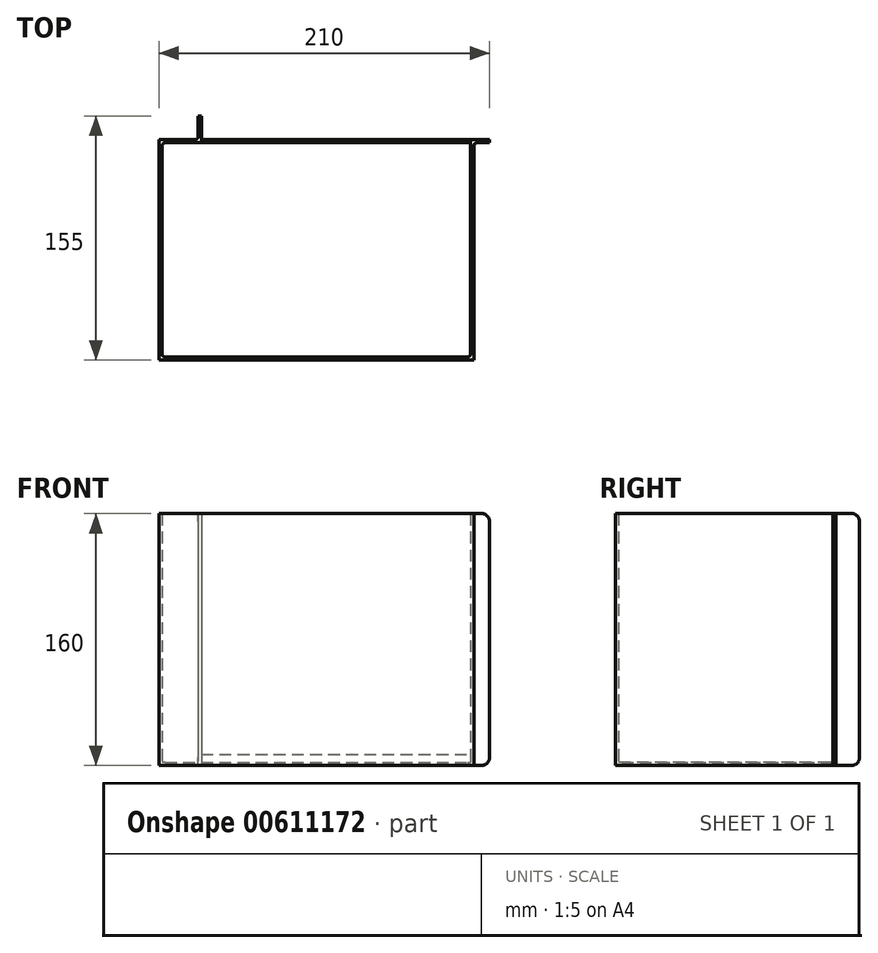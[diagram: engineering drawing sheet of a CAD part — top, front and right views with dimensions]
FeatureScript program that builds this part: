
annotation { "Feature Type Name" : "Feature", "Feature Type Description" : "" }
export const myFeature = defineFeature(function(context is Context, id is Id, definition is map)
    precondition{}
    {
        {
            var Q0;
            Q0=qCreatedBy(makeId("Top.planeOp"),FACE);
            var sketch = newSketch(context, id + "F0", { "sketchPlane" : qUnion([Q0])});
            skLineSegment(sketch, "E0.bottom", {"start": v(-131.14, 84.52) * mm, "end": v(-106.14, 84.52) * mm});
            skLineSegment(sketch, "E0.top", {"start": v(-131.14, -55.48) * mm, "end": v(68.86, -55.48) * mm});
            skLineSegment(sketch, "E0.left", {"start": v(-131.14, 84.52) * mm, "end": v(-131.14, -55.48) * mm});
            skLineSegment(sketch, "E0.right", {"start": v(68.86, 84.52) * mm, "end": v(68.86, -55.48) * mm});
            skLineSegment(sketch, "E1", {"start": v(-129.14, 82.52) * mm, "end": v(-129.14, -53.48) * mm});
            skLineSegment(sketch, "E2", {"start": v(-129.14, -53.48) * mm, "end": v(66.86, -53.48) * mm});
            skLineSegment(sketch, "E3", {"start": v(66.86, -53.48) * mm, "end": v(66.86, 84.52) * mm});
            skLineSegment(sketch, "E4", {"start": v(-129.14, 82.52) * mm, "end": v(-104.14, 82.52) * mm});
            skLineSegment(sketch, "E5", {"start": v(-104.14, 82.52) * mm, "end": v(-104.14, 84.52) * mm});
            skLineSegment(sketch, "E6", {"start": v(-104.14, 84.52) * mm, "end": v(-104.14, 99.52) * mm});
            skLineSegment(sketch, "E7", {"start": v(-104.14, 99.52) * mm, "end": v(-106.14, 99.52) * mm});
            skLineSegment(sketch, "E8", {"start": v(-106.14, 99.52) * mm, "end": v(-106.14, 84.52) * mm});
            skLineSegment(sketch, "E9.trimOffspring", {"start": v(-104.14, 84.52) * mm, "end": v(68.86, 84.52) * mm});
            skLineSegment(sketch, "E10", {"start": v(-104.14, 82.52) * mm, "end": v(66.86, 82.52) * mm});
            skLineSegment(sketch, "E11.bottom", {"start": v(68.86, 84.52) * mm, "end": v(78.86, 84.52) * mm});
            skLineSegment(sketch, "E11.top", {"start": v(68.86, 82.52) * mm, "end": v(78.86, 82.52) * mm});
            skLineSegment(sketch, "E11.left", {"start": v(68.86, 84.52) * mm, "end": v(68.86, 82.52) * mm});
            skLineSegment(sketch, "E11.right", {"start": v(78.86, 84.52) * mm, "end": v(78.86, 82.52) * mm});
            skSolve(sketch);
        }
        {
            var Q0;
            Q0=makeQuery(id+"F0.imprint","IMPRINT",FACE,{"disambiguationData":[TD([[makeQuery(id+"F0.imprint","IMPRINT",EDGE,{"derivedFrom":sQuery(id+"F0.wireOp",EDGE,"E0.bottom")}),-1.0]])]});
            var Q1;
            Q1=makeQuery(id+"F0.imprint","IMPRINT",FACE,{"disambiguationData":[TD([[makeQuery(id+"F0.imprint","IMPRINT",EDGE,{"derivedFrom":sQuery(id+"F0.wireOp",EDGE,"E11.bottom")}),-1.0]])]});
            extrude(context, id + "F1", {"entities" : qUnion([Q0, Q1]), "depth" : 160 * mm, "offsetDistance" : 25 * mm});
        }
        {
            var Q0;
            {var subQ4=sQuery(id+"F0.wireOp",EDGE,"E5");Q0=makeQuery(id+"F0.imprint","IMPRINT",FACE,{"disambiguationData":[TD([[makeQuery(id+"F0.imprint","IMPRINT",EDGE,{"derivedFrom":subQ4}),-1.0]])]});}
            extrude(context, id + "F2", {"entities" : qUnion([Q0]), "operationType" : NewBodyOperationType.ADD, "depth" : 7 * mm, "offsetDistance" : 25 * mm});
        }
        {
            var Q0;
            Q0=makeQuery(id+"F0.imprint","IMPRINT",FACE,{"disambiguationData":[TD([[makeQuery(id+"F0.imprint","IMPRINT",EDGE,{"derivedFrom":sQuery(id+"F0.wireOp",EDGE,"E1")}),1.0]])]});
            extrude(context, id + "F3", {"entities" : qUnion([Q0]), "operationType" : NewBodyOperationType.ADD, "depth" : 2 * mm, "offsetDistance" : 25 * mm});
        }
        {
            var Q0;
            Q0=makeQuery(id+"F1.opExtrude","CAP_EDGE",EDGE,{"disambiguationData":[OSD([sQuery(id+"F0.wireOp",EDGE,"E7")])],"isStart":false});
            var Q1;
            Q1=makeQuery(id+"F1.opExtrude","CAP_EDGE",EDGE,{"disambiguationData":[OSD([sQuery(id+"F0.wireOp",EDGE,"E7")])],"isStart":true});
            var Q2;
            Q2=makeQuery(id+"F1.opExtrude","CAP_EDGE",EDGE,{"disambiguationData":[OSD([sQuery(id+"F0.wireOp",EDGE,"E11.right")])],"isStart":true});
            var Q3;
            Q3=makeQuery(id+"F1.opExtrude","CAP_EDGE",EDGE,{"disambiguationData":[OSD([sQuery(id+"F0.wireOp",EDGE,"E11.right")])],"isStart":false});
            fillet(context, id + "F4", {"entities" : qUnion([Q0, Q1, Q2, Q3]), "radius" : 5 * mm, "tangentPropagation" : true, "allowEdgeOverflow" : false});
        }
        {
            var Q0;
            Q0=makeQuery(id+"F1.opExtrude","SWEPT_EDGE",EDGE,{"disambiguationData":[OSD([sQuery(id+"F0.wireOp",EDGE,"E1"),sQuery(id+"F0.wireOp",EDGE,"E2")])]});
            var Q1;
            Q1=makeQuery(id+"F3.opExtrude","CAP_EDGE",EDGE,{"disambiguationData":[OSD([sQuery(id+"F0.wireOp",EDGE,"E2")])],"isStart":false});
            var Q2;
            Q2=makeQuery(id+"F3.opExtrude","CAP_EDGE",EDGE,{"disambiguationData":[OSD([sQuery(id+"F0.wireOp",EDGE,"E1")])],"isStart":false});
            var Q3;
            Q3=makeQuery(id+"F3.opExtrude","CAP_EDGE",EDGE,{"disambiguationData":[OSD([sQuery(id+"F0.wireOp",EDGE,"E3")])],"isStart":false});
            var Q4;
            Q4=makeQuery(id+"F1.opExtrude","SWEPT_EDGE",EDGE,{"disambiguationData":[OSD([sQuery(id+"F0.wireOp",EDGE,"E2"),sQuery(id+"F0.wireOp",EDGE,"E3")])]});
            var Q5;
            Q5=makeQuery(id+"F1.opExtrude","SWEPT_EDGE",EDGE,{"disambiguationData":[OSD([sQuery(id+"F0.wireOp",EDGE,"E1"),sQuery(id+"F0.wireOp",EDGE,"E4")])]});
            var Q6;
            Q6=makeQuery(id+"F3.opExtrude","CAP_EDGE",EDGE,{"disambiguationData":[OSD([sQuery(id+"F0.wireOp",EDGE,"E4"),sQuery(id+"F0.wireOp",EDGE,"E10")])],"isStart":false});
            var Q7;
            Q7=makeQuery(id+"F1.opExtrude","SWEPT_EDGE",EDGE,{"disambiguationData":[OSD([sQuery(id+"F0.wireOp",EDGE,"E0.right"),sQuery(id+"F0.wireOp",EDGE,"E11.top"),sQuery(id+"F0.wireOp",EDGE,"E11.left")])]});
            var Q8;
            Q8=makeQuery(id+"F1.opExtrude","SWEPT_EDGE",EDGE,{"disambiguationData":[OSD([sQuery(id+"F0.wireOp",EDGE,"E0.bottom"),sQuery(id+"F0.wireOp",EDGE,"E8")])]});
            fillet(context, id + "F5", {"entities" : qUnion([Q0, Q1, Q2, Q3, Q4, Q5, Q6, Q7, Q8]), "radius" : 2 * mm, "tangentPropagation" : true, "allowEdgeOverflow" : false});
        }
    });
